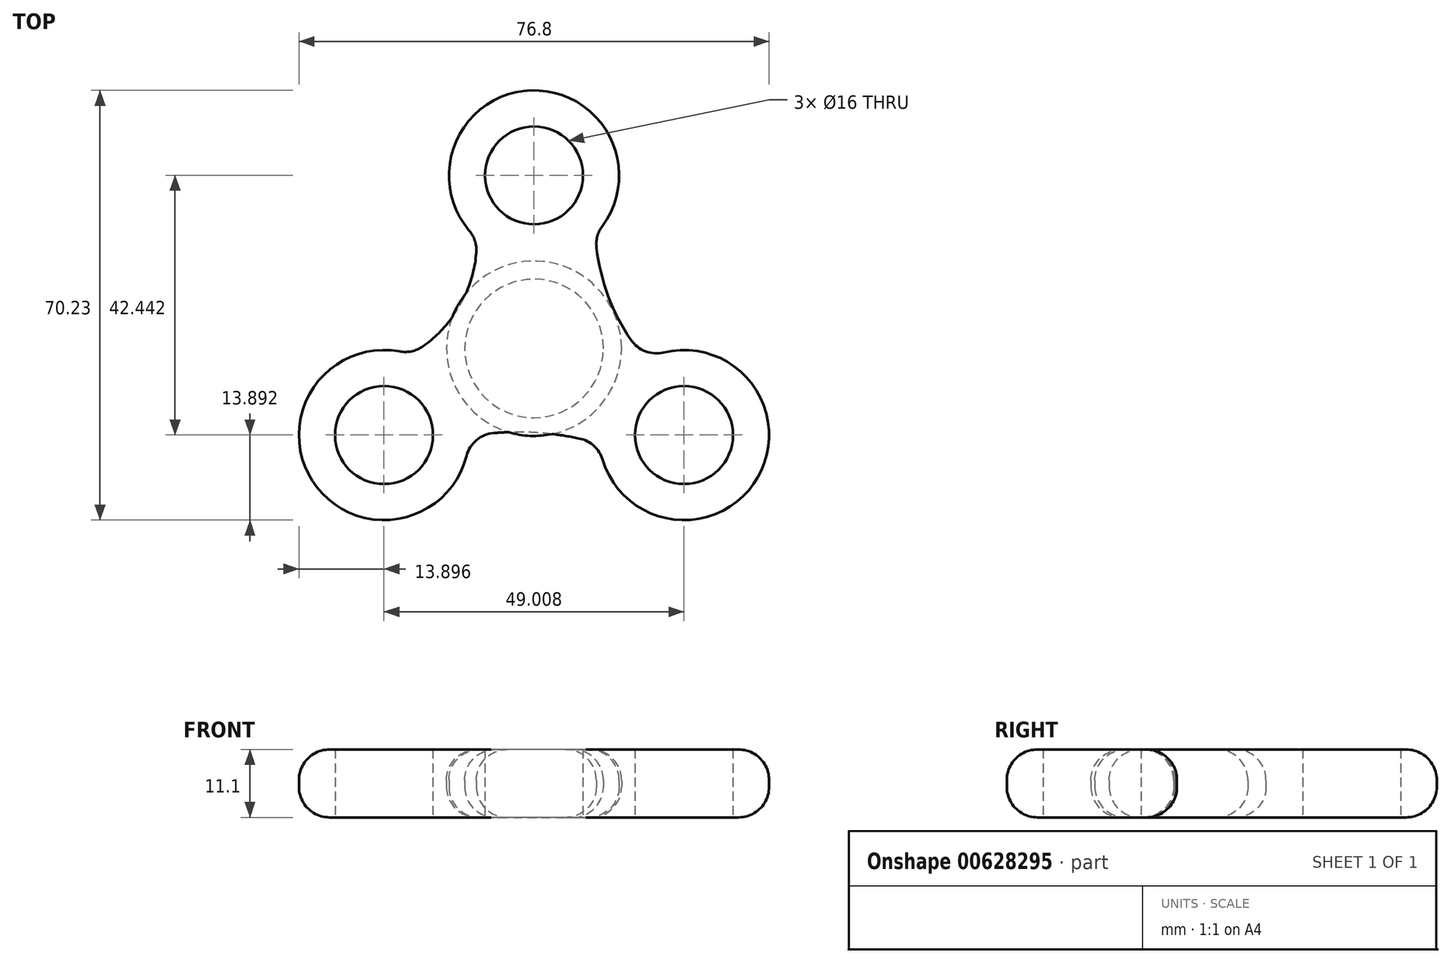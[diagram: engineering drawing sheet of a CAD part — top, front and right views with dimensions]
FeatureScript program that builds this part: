
annotation { "Feature Type Name" : "Feature", "Feature Type Description" : "" }
export const myFeature = defineFeature(function(context is Context, id is Id, definition is map)
    precondition{}
    {
        {
            var Q0;
            Q0=qCreatedBy(makeId("Top.planeOp"),FACE);
            var sketch = newSketch(context, id + "F0", { "sketchPlane" : qUnion([Q0])});
            skCircle(sketch, "E0", {"center": v(0, 0) * mm, "radius": 11.32 * mm});
            skSolve(sketch);
        }
        {
            var Q0;
            Q0=qCreatedBy(makeId("Top.planeOp"),FACE);
            var sketch = newSketch(context, id + "F1", { "sketchPlane" : qUnion([Q0])});
            skCircle(sketch, "E1", {"center": v(0, 0) * mm, "radius": 14.3 * mm});
            skSolve(sketch);
        }
        {
            var Q0;
            Q0=qCreatedBy(makeId("Top.planeOp"),FACE);
            var sketch = newSketch(context, id + "F2", { "sketchPlane" : qUnion([Q0])});
            skCircle(sketch, "E2", {"center": v(0, 28.3) * mm, "radius": 10.81 * mm});
            skCircle(sketch, "E3", {"center": v(0, 28.3) * mm, "radius": 13.9 * mm});
            skCircle(sketch, "E4.1.0", {"center": v(-24.5, -14.15) * mm, "radius": 13.9 * mm});
            skCircle(sketch, "E4.1.1", {"center": v(-24.5, -14.15) * mm, "radius": 10.81 * mm});
            skCircle(sketch, "E4.2.0", {"center": v(24.5, -14.15) * mm, "radius": 13.9 * mm});
            skCircle(sketch, "E4.2.1", {"center": v(24.5, -14.15) * mm, "radius": 10.81 * mm});
            skPoint(sketch, "E4.center", {"position": v(0, 0) * mm});
            skArc(sketch, "E5", {"start": v(-20.19, -0.94) * mm, "mid": v(-12.11, 7.02) * mm, "end": v(-9.36, 18.02) * mm});
            skArc(sketch, "E6", {"start": v(10, 18.65) * mm, "mid": v(12.43, 7.77) * mm, "end": v(18.27, -1.73) * mm});
            skArc(sketch, "E7", {"start": v(10.68, -15.52) * mm, "mid": v(0.1, -13.74) * mm, "end": v(-10.6, -14.3) * mm});
            skSolve(sketch);
        }
        {
            var Q0;
            Q0=makeQuery(id+"F1.imprint","IMPRINT",FACE,{"disambiguationData":[TD([[makeQuery(id+"F1.imprint","IMPRINT",EDGE,{"derivedFrom":sQuery(id+"F1.wireOp",EDGE,"E1")}),1.0]])]});
            var Q1;
            Q1=makeQuery(id+"F0.imprint","IMPRINT",FACE,{"disambiguationData":[TD([[makeQuery(id+"F0.imprint","IMPRINT",EDGE,{"derivedFrom":sQuery(id+"F0.wireOp",EDGE,"E0")}),1.0]])]});
            var Q2;
            Q2=makeQuery(id+"F2.imprint","IMPRINT",FACE,{"disambiguationData":[TD([[makeQuery(id+"F2.imprint","IMPRINT",EDGE,{"derivedFrom":sQuery(id+"F2.wireOp",EDGE,"E2")}),1.0]])]});
            var Q3;
            Q3=makeQuery(id+"F2.imprint","IMPRINT",FACE,{"disambiguationData":[TD([[makeQuery(id+"F2.imprint","IMPRINT",EDGE,{"derivedFrom":sQuery(id+"F2.wireOp",EDGE,"E4.1.1")}),1.0]])]});
            var Q4;
            Q4=makeQuery(id+"F2.imprint","IMPRINT",FACE,{"disambiguationData":[TD([[makeQuery(id+"F2.imprint","IMPRINT",EDGE,{"derivedFrom":sQuery(id+"F2.wireOp",EDGE,"E4.2.1")}),1.0]])]});
            var Q5;
            Q5=makeQuery(id+"F2.imprint","IMPRINT",FACE,{"disambiguationData":[TD([[makeQuery(id+"F2.imprint","IMPRINT",EDGE,{"derivedFrom":sQuery(id+"F2.wireOp",EDGE,"E2")}),-1.0]])]});
            var Q6;
            Q6=makeQuery(id+"F2.imprint","IMPRINT",FACE,{"disambiguationData":[TD([[makeQuery(id+"F2.imprint","IMPRINT",EDGE,{"derivedFrom":sQuery(id+"F2.wireOp",EDGE,"E4.1.1")}),-1.0]])]});
            var Q7;
            Q7=makeQuery(id+"F2.imprint","IMPRINT",FACE,{"disambiguationData":[TD([[makeQuery(id+"F2.imprint","IMPRINT",EDGE,{"derivedFrom":sQuery(id+"F2.wireOp",EDGE,"E4.2.1")}),-1.0]])]});
            var Q8;
            {var subQ0=sQuery(id+"F2.wireOp",EDGE,"E5");Q8=makeQuery(id+"F2.imprint","IMPRINT",FACE,{"disambiguationData":[TD([[makeQuery(id+"F2.imprint","IMPRINT",EDGE,{"derivedFrom":subQ0}),-1.0]])]});}
            extrude(context, id + "F3", {"entities" : qUnion([Q0, Q1, Q2, Q3, Q4, Q5, Q6, Q7, Q8]), "depth" : 11.1 * mm, "offsetDistance" : 25 * mm});
        }
        {
            var Q0;
            Q0=makeQuery(id+"F3.opExtrude","SWEPT_EDGE",EDGE,{"disambiguationData":[OSD([sQuery(id+"F2.wireOp",EDGE,"E3"),sQuery(id+"F2.wireOp",EDGE,"E5")])]});
            var Q1;
            Q1=makeQuery(id+"F3.opExtrude","SWEPT_EDGE",EDGE,{"disambiguationData":[OSD([sQuery(id+"F2.wireOp",EDGE,"E3"),sQuery(id+"F2.wireOp",EDGE,"E6")])]});
            var Q2;
            Q2=makeQuery(id+"F3.opExtrude","CAP_EDGE",EDGE,{"disambiguationData":[OSD([sQuery(id+"F2.wireOp",EDGE,"E5")])],"isStart":true});
            var Q3;
            Q3=makeQuery(id+"F3.opExtrude","CAP_EDGE",EDGE,{"disambiguationData":[OSD([sQuery(id+"F2.wireOp",EDGE,"E6")])],"isStart":true});
            var Q4;
            Q4=makeQuery(id+"F3.opExtrude","CAP_FACE",FACE,{"disambiguationData":[OSD([sQuery(id+"F1.wireOp",EDGE,"E1")])],"isStart":false});
            var Q5;
            Q5=makeQuery(id+"F3.opExtrude","SWEPT_FACE",FACE,{"disambiguationData":[OSD([sQuery(id+"F1.wireOp",EDGE,"E1")])]});
            var Q6;
            Q6=makeQuery(id+"F3.opExtrude","CAP_EDGE",EDGE,{"disambiguationData":[OSD([sQuery(id+"F1.wireOp",EDGE,"E1")])],"isStart":false});
            var Q7;
            Q7=makeQuery(id+"F3.opExtrude","CAP_EDGE",EDGE,{"disambiguationData":[OSD([sQuery(id+"F2.wireOp",EDGE,"E4.2.0")])],"isStart":false});
            var Q8;
            Q8=makeQuery(id+"F3.opExtrude","CAP_EDGE",EDGE,{"disambiguationData":[OSD([sQuery(id+"F2.wireOp",EDGE,"E4.2.0")])],"isStart":true});
            var Q9;
            Q9=makeQuery(id+"F3.opExtrude","CAP_EDGE",EDGE,{"disambiguationData":[OSD([sQuery(id+"F2.wireOp",EDGE,"E4.1.0")])],"isStart":false});
            var Q10;
            Q10=makeQuery(id+"F3.opExtrude","SWEPT_FACE",FACE,{"disambiguationData":[OSD([sQuery(id+"F2.wireOp",EDGE,"E3")])]});
            var Q11;
            Q11=makeQuery(id+"F3.opExtrude","CAP_FACE",FACE,{"disambiguationData":[OSD([sQuery(id+"F2.wireOp",EDGE,"E3"),sQuery(id+"F2.wireOp",EDGE,"E4.1.0"),sQuery(id+"F2.wireOp",EDGE,"E4.2.0"),sQuery(id+"F2.wireOp",EDGE,"E5"),sQuery(id+"F2.wireOp",EDGE,"E6"),sQuery(id+"F2.wireOp",EDGE,"E7")])],"isStart":true});
            var Q12;
            Q12=makeQuery(id+"F3.opExtrude","CAP_FACE",FACE,{"disambiguationData":[OSD([sQuery(id+"F2.wireOp",EDGE,"E3"),sQuery(id+"F2.wireOp",EDGE,"E4.1.0"),sQuery(id+"F2.wireOp",EDGE,"E4.2.0"),sQuery(id+"F2.wireOp",EDGE,"E5"),sQuery(id+"F2.wireOp",EDGE,"E6"),sQuery(id+"F2.wireOp",EDGE,"E7")])],"isStart":false});
            var Q13;
            Q13=makeQuery(id+"F3.opExtrude","SWEPT_FACE",FACE,{"disambiguationData":[OSD([sQuery(id+"F2.wireOp",EDGE,"E4.1.0")])]});
            var Q14;
            Q14=makeQuery(id+"F3.opExtrude","CAP_EDGE",EDGE,{"disambiguationData":[OSD([sQuery(id+"F2.wireOp",EDGE,"E3")])],"isStart":true});
            var Q15;
            Q15=makeQuery(id+"F3.opExtrude","SWEPT_FACE",FACE,{"disambiguationData":[OSD([sQuery(id+"F2.wireOp",EDGE,"E4.2.0")])]});
            var Q16;
            Q16=makeQuery(id+"F3.opExtrude","CAP_EDGE",EDGE,{"disambiguationData":[OSD([sQuery(id+"F2.wireOp",EDGE,"E3")])],"isStart":false});
            var Q17;
            Q17=makeQuery(id+"F3.opExtrude","SWEPT_FACE",FACE,{"disambiguationData":[OSD([sQuery(id+"F2.wireOp",EDGE,"E6")])]});
            var Q18;
            Q18=makeQuery(id+"F3.opExtrude","CAP_EDGE",EDGE,{"disambiguationData":[OSD([sQuery(id+"F2.wireOp",EDGE,"E5")])],"isStart":false});
            var Q19;
            Q19=makeQuery(id+"F3.opExtrude","CAP_EDGE",EDGE,{"disambiguationData":[OSD([sQuery(id+"F2.wireOp",EDGE,"E6")])],"isStart":false});
            var Q20;
            Q20=makeQuery(id+"F3.opExtrude","CAP_EDGE",EDGE,{"disambiguationData":[OSD([sQuery(id+"F2.wireOp",EDGE,"E7")])],"isStart":false});
            var Q21;
            Q21=makeQuery(id+"F3.opExtrude","SWEPT_FACE",FACE,{"disambiguationData":[OSD([sQuery(id+"F0.wireOp",EDGE,"E0")])]});
            var Q22;
            Q22=makeQuery(id+"F3.opExtrude","CAP_EDGE",EDGE,{"disambiguationData":[OSD([sQuery(id+"F0.wireOp",EDGE,"E0")])],"isStart":false});
            var Q23;
            Q23=makeQuery(id+"F3.opExtrude","CAP_FACE",FACE,{"disambiguationData":[OSD([sQuery(id+"F0.wireOp",EDGE,"E0")])],"isStart":false});
            var Q24;
            Q24=makeQuery(id+"F3.opExtrude","CAP_FACE",FACE,{"disambiguationData":[OSD([sQuery(id+"F1.wireOp",EDGE,"E1")])],"isStart":true});
            var Q25;
            Q25=makeQuery(id+"F3.opExtrude","CAP_EDGE",EDGE,{"disambiguationData":[OSD([sQuery(id+"F1.wireOp",EDGE,"E1")])],"isStart":true});
            var Q26;
            Q26=makeQuery(id+"F3.opExtrude","SWEPT_FACE",FACE,{"disambiguationData":[OSD([sQuery(id+"F2.wireOp",EDGE,"E7")])]});
            var Q27;
            Q27=makeQuery(id+"F3.opExtrude","SWEPT_EDGE",EDGE,{"disambiguationData":[OSD([sQuery(id+"F2.wireOp",EDGE,"E4.1.0"),sQuery(id+"F2.wireOp",EDGE,"E5")])]});
            var Q28;
            Q28=makeQuery(id+"F3.opExtrude","SWEPT_EDGE",EDGE,{"disambiguationData":[OSD([sQuery(id+"F2.wireOp",EDGE,"E4.2.0"),sQuery(id+"F2.wireOp",EDGE,"E6")])]});
            var Q29;
            Q29=makeQuery(id+"F3.opExtrude","SWEPT_EDGE",EDGE,{"disambiguationData":[OSD([sQuery(id+"F2.wireOp",EDGE,"E4.2.0"),sQuery(id+"F2.wireOp",EDGE,"E7")])]});
            var Q30;
            Q30=makeQuery(id+"F3.opExtrude","SWEPT_FACE",FACE,{"disambiguationData":[OSD([sQuery(id+"F2.wireOp",EDGE,"E5")])]});
            var Q31;
            Q31=makeQuery(id+"F3.opExtrude","CAP_EDGE",EDGE,{"disambiguationData":[OSD([sQuery(id+"F2.wireOp",EDGE,"E4.1.0")])],"isStart":true});
            var Q32;
            Q32=makeQuery(id+"F3.opExtrude","CAP_EDGE",EDGE,{"disambiguationData":[OSD([sQuery(id+"F0.wireOp",EDGE,"E0")])],"isStart":true});
            var Q33;
            Q33=makeQuery(id+"F3.opExtrude","CAP_FACE",FACE,{"disambiguationData":[OSD([sQuery(id+"F0.wireOp",EDGE,"E0")])],"isStart":true});
            var Q34;
            Q34=makeQuery(id+"F3.opExtrude","SWEPT_EDGE",EDGE,{"disambiguationData":[OSD([sQuery(id+"F2.wireOp",EDGE,"E4.1.0"),sQuery(id+"F2.wireOp",EDGE,"E7")])]});
            var Q35;
            Q35=makeQuery(id+"F3.opExtrude","CAP_EDGE",EDGE,{"disambiguationData":[OSD([sQuery(id+"F2.wireOp",EDGE,"E7")])],"isStart":true});
            fillet(context, id + "F4", {"entities" : qUnion([Q0, Q1, Q2, Q3, Q4, Q5, Q6, Q7, Q8, Q9, Q10, Q11, Q12, Q13, Q14, Q15, Q16, Q17, Q18, Q19, Q20, Q21, Q22, Q23, Q24, Q25, Q26, Q27, Q28, Q29, Q30, Q31, Q32, Q33, Q34, Q35]), "radius" : 5 * mm, "tangentPropagation" : true, "allowEdgeOverflow" : false});
        }
        {
            var Q0;
            Q0=sQuery(id+"F2.wireOp",VERTEX,"E4.2.0.center");
            var Q1;
            Q1=sQuery(id+"F2.wireOp",VERTEX,"E2.center");
            var Q2;
            Q2=sQuery(id+"F2.wireOp",VERTEX,"E4.1.1.center");
            var Q3;
            Q3=makeQuery(id+"F3.opExtrude","SWEPT_BODY",BODY,{"disambiguationData":[OSD([sQuery(id+"F2.wireOp",EDGE,"E3"),sQuery(id+"F2.wireOp",EDGE,"E4.1.0"),sQuery(id+"F2.wireOp",EDGE,"E4.2.0"),sQuery(id+"F2.wireOp",EDGE,"E5"),sQuery(id+"F2.wireOp",EDGE,"E6"),sQuery(id+"F2.wireOp",EDGE,"E7")])]});
            hole(context, id + "F5", {"style" : HoleStyle.SIMPLE, "endStyle" : HoleEndStyle.THROUGH, "oppositeDirection" : true, "holeDiameter" : 16 * mm, "majorDiameter" : 5 * mm, "isTappedThrough" : true, "tappedDepth" : 12 * mm, "tapClearance" : 3, "locations" : qUnion([Q0, Q1, Q2]), "scope" : qUnion([Q3])});
        }
    });
